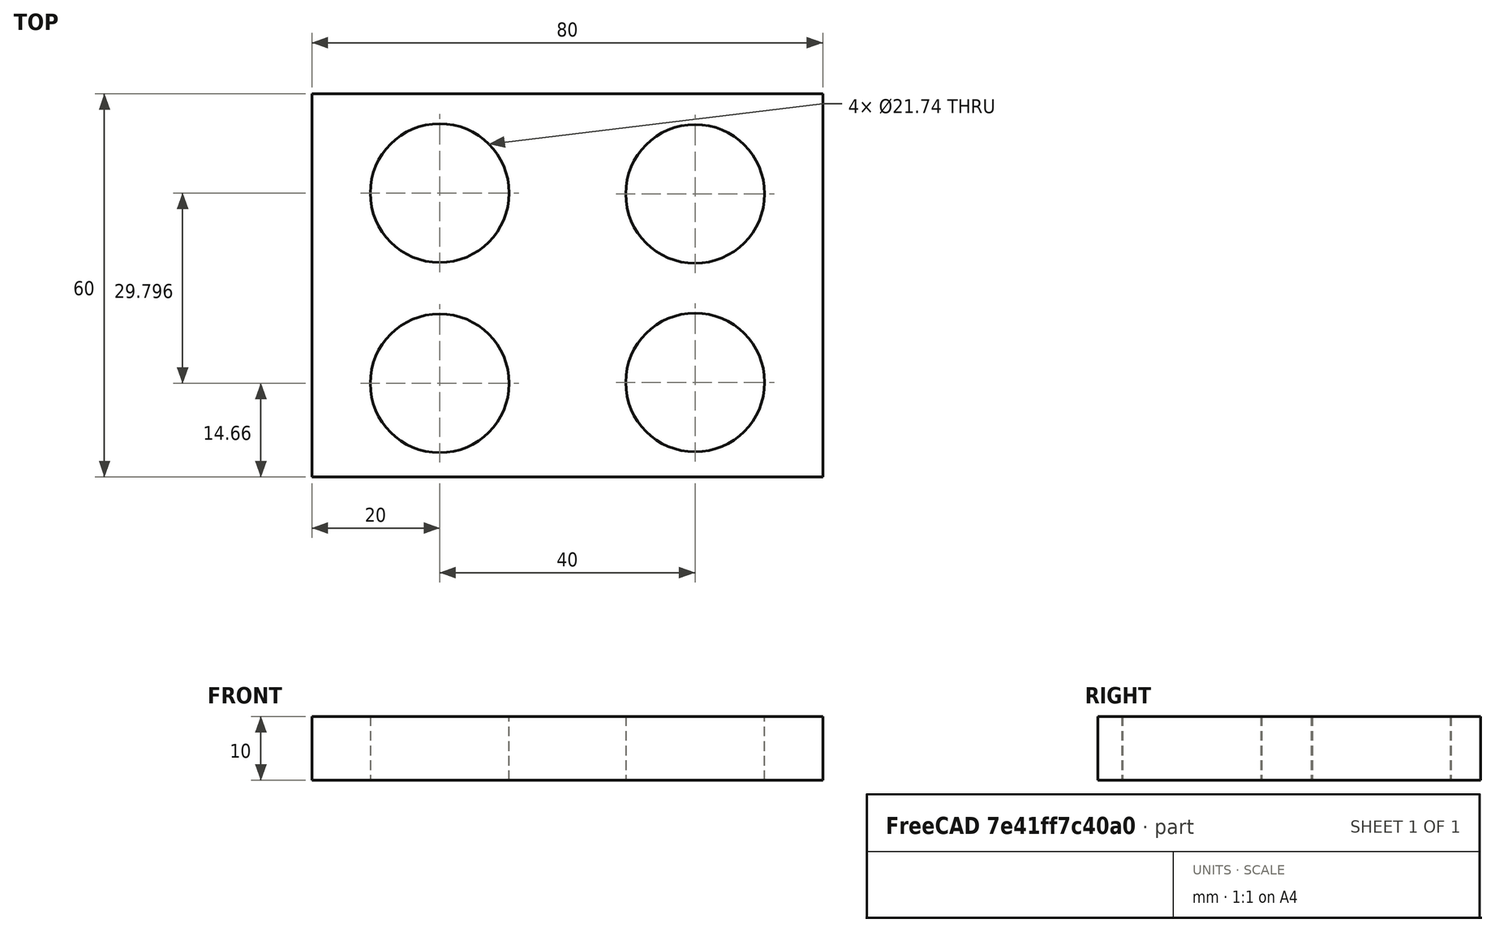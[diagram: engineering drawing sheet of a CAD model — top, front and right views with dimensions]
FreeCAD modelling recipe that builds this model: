
FCSTD DOCUMENT  (FreeCAD 0.20R29177 (Git))
Label: test1
License: All rights reserved
LicenseURL: http://en.wikipedia.org/wiki/All_rights_reserved
objects: Sketcher::SketchObject×1, PartDesign::Pad×1, PartDesign::Body×1
note: 4 computed .brp shape members not serialized (recipe doc carries the construction recipe); baked Part::Feature solids carry a one-line shape summary decoded from their .brp

FEATURE [Sketcher::SketchObject] Sketch
  FullyConstrained = false
  MapMode = 5
  Support = -> [XY_Plane]
  sketch-geometry (8):
    g0: LineSegment StartX=-40 StartY=30 StartZ=0 EndX=40 EndY=30 EndZ=0
    g1: LineSegment StartX=40 StartY=30 StartZ=0 EndX=40 EndY=-30 EndZ=0
    g2: LineSegment StartX=40 StartY=-30 StartZ=0 EndX=-40 EndY=-30 EndZ=0
    g3: LineSegment StartX=-40 StartY=-30 StartZ=0 EndX=-40 EndY=30 EndZ=0
    g4: Circle CenterX=20 CenterY=14.3237 CenterZ=0 NormalX=0 NormalY=0 NormalZ=1 AngleXU=0 Radius=10.8683
    g5: Circle CenterX=20 CenterY=-15.2086 CenterZ=0 NormalX=0 NormalY=0 NormalZ=1 AngleXU=0 Radius=10.8683
    g6: Circle CenterX=-20 CenterY=14.4556 CenterZ=0 NormalX=0 NormalY=0 NormalZ=1 AngleXU=0 Radius=10.8683
    g7: Circle CenterX=-20 CenterY=-15.3404 CenterZ=0 NormalX=0 NormalY=0 NormalZ=1 AngleXU=0 Radius=10.8683
  constraints (12):
    c: Symmetric(g0,g0,g-2)
    c: Symmetric(g2,g1,g-2)
    c: Symmetric(g1,g1,g-1)
    c: Symmetric(g3,g3,g-1)
    c: Coincident(g3,g0)
    c: Coincident(g2,g1)
    c: Coincident(g3,g2)
    c: DistanceX(g0,g0) = 80
    c: DistanceY(g3,g3) = 60
    c: Equal(g6,g7)
    c: Equal(g4,g5)
    c: Equal(g7,g5)
FEATURE [PartDesign::Pad] Pad
  Direction = (0,0,1)
  Length = 10
  Length2 = 10
  Profile = -> Sketch
  ReferenceAxis = -> Sketch [N_Axis]
  Type = 0
FEATURE [PartDesign::Body] Body
  Group = -> [Sketch,Pad]
  Origin = -> Origin
  Tip = -> Pad
